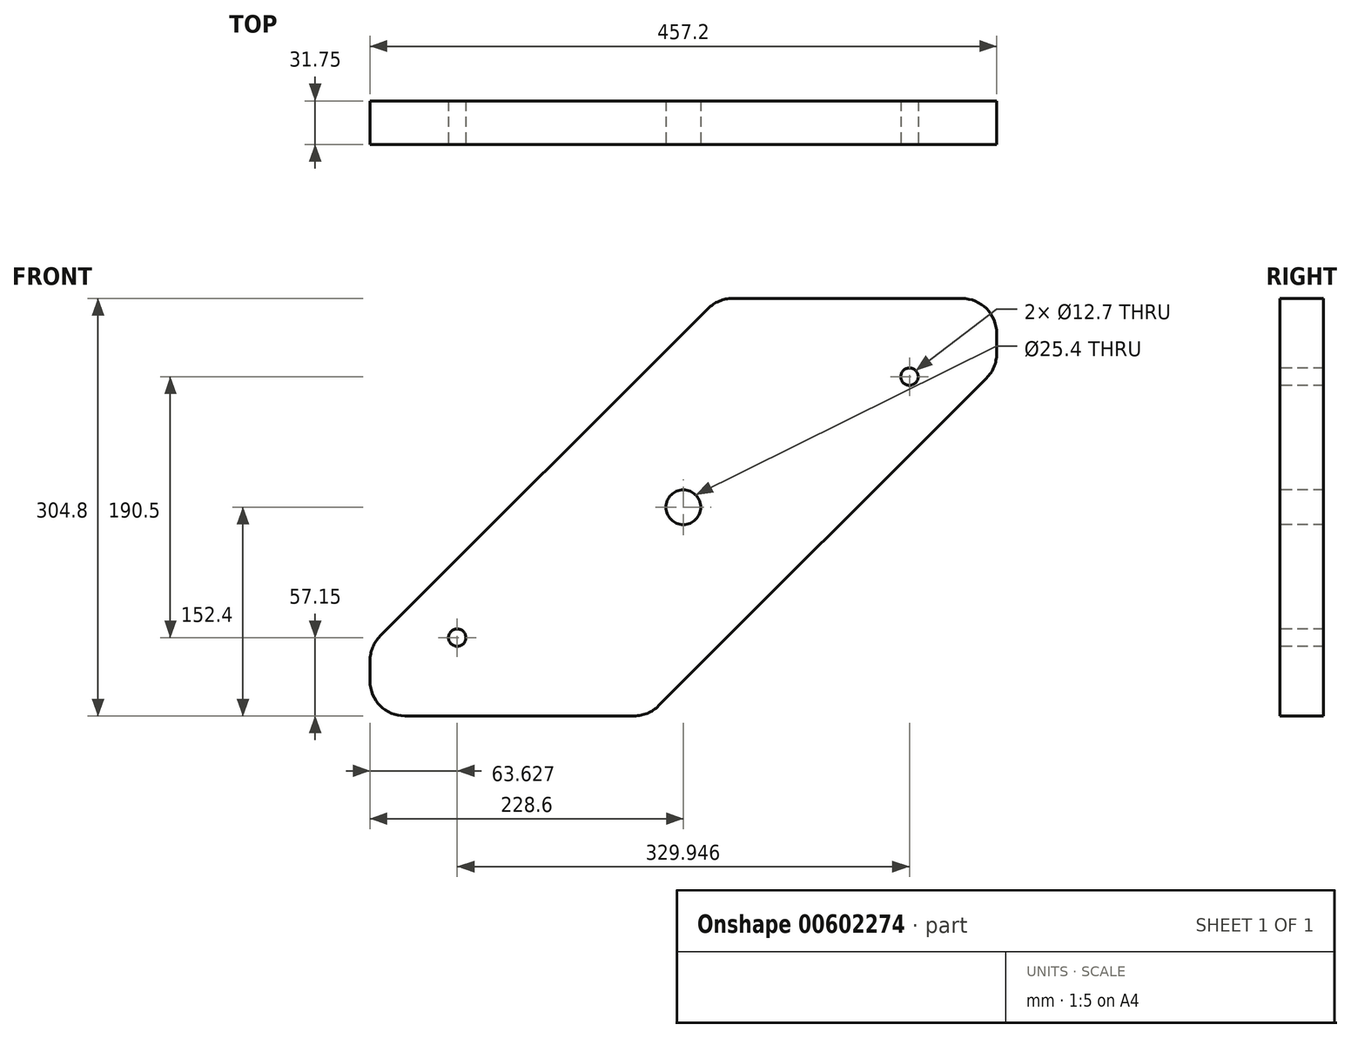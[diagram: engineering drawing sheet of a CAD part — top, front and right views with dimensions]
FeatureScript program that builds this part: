
annotation { "Feature Type Name" : "Feature", "Feature Type Description" : "" }
export const myFeature = defineFeature(function(context is Context, id is Id, definition is map)
    precondition{}
    {
        {
            var Q0;
            Q0=qCreatedBy(makeId("Front.planeOp"),FACE);
            var sketch = newSketch(context, id + "F0", { "sketchPlane" : qUnion([Q0])});
            skLineSegment(sketch, "E0.bottom", {"start": v(0, 0) * mm, "end": v(457.2, 0) * mm});
            skLineSegment(sketch, "E0.top", {"start": v(0, 304.8) * mm, "end": v(457.2, 304.8) * mm});
            skLineSegment(sketch, "E0.left", {"start": v(0, 0) * mm, "end": v(0, 304.8) * mm});
            skLineSegment(sketch, "E0.right", {"start": v(457.2, 0) * mm, "end": v(457.2, 304.8) * mm});
            skSolve(sketch);
        }
        {
            var Q0;
            Q0 = qSketchRegion(id + "F0", true);
            extrude(context, id + "F1", {"entities" : qUnion([Q0]), "depth" : 31.75 * mm, "offsetDistance" : 25.4 * mm});
        }
        {
            var Q0;
            Q0=makeQuery(id+"F1.opExtrude","SWEPT_EDGE",EDGE,{"disambiguationData":[OSD([sQuery(id+"F0.wireOp",EDGE,"E0.top"),sQuery(id+"F0.wireOp",EDGE,"E0.left")])]});
            var Q1;
            Q1=makeQuery(id+"F1.opExtrude","SWEPT_EDGE",EDGE,{"disambiguationData":[OSD([sQuery(id+"F0.wireOp",EDGE,"E0.bottom"),sQuery(id+"F0.wireOp",EDGE,"E0.right")])]});
            chamfer(context, id + "F2", {"entities" : qUnion([Q0, Q1]), "chamferType" : ChamferType.OFFSET_ANGLE, "width" : 254 * mm, "oppositeDirection" : false, "angle" : 45 * degree, "tangentPropagation" : true});
        }
        {
            var Q0;
            {var subQ0=sQuery(id+"F0.wireOp",EDGE,"E0.left");Q0=makeQuery(id+"F2.opChamfer","BLEND_EDGE",EDGE,{"blendedFrom":[makeQuery(id+"F1.opExtrude","SWEPT_EDGE",EDGE,{"disambiguationData":[OSD([sQuery(id+"F0.wireOp",EDGE,"E0.top"),subQ0])]}),makeQuery(id+"F1.opExtrude","SWEPT_FACE",FACE,{"disambiguationData":[OSD([subQ0])]})],"blendedInto":[makeQuery(id+"F1.opExtrude","SWEPT_FACE",FACE,{"disambiguationData":[OSD([subQ0])]})]});}
            var Q1;
            Q1=makeQuery(id+"F1.opExtrude","SWEPT_EDGE",EDGE,{"disambiguationData":[OSD([sQuery(id+"F0.wireOp",EDGE,"E0.bottom"),sQuery(id+"F0.wireOp",EDGE,"E0.left")])]});
            var Q2;
            {var subQ0=sQuery(id+"F0.wireOp",EDGE,"E0.bottom");Q2=makeQuery(id+"F2.opChamfer","BLEND_EDGE",EDGE,{"blendedFrom":[makeQuery(id+"F1.opExtrude","SWEPT_EDGE",EDGE,{"disambiguationData":[OSD([subQ0,sQuery(id+"F0.wireOp",EDGE,"E0.right")])]}),makeQuery(id+"F1.opExtrude","SWEPT_FACE",FACE,{"disambiguationData":[OSD([subQ0])]})],"blendedInto":[makeQuery(id+"F1.opExtrude","SWEPT_FACE",FACE,{"disambiguationData":[OSD([subQ0])]})]});}
            var Q3;
            {var subQ0=sQuery(id+"F0.wireOp",EDGE,"E0.right");Q3=makeQuery(id+"F2.opChamfer","BLEND_EDGE",EDGE,{"blendedFrom":[makeQuery(id+"F1.opExtrude","SWEPT_EDGE",EDGE,{"disambiguationData":[OSD([sQuery(id+"F0.wireOp",EDGE,"E0.bottom"),subQ0])]}),makeQuery(id+"F1.opExtrude","SWEPT_FACE",FACE,{"disambiguationData":[OSD([subQ0])]})],"blendedInto":[makeQuery(id+"F1.opExtrude","SWEPT_FACE",FACE,{"disambiguationData":[OSD([subQ0])]})]});}
            var Q4;
            Q4=makeQuery(id+"F1.opExtrude","SWEPT_EDGE",EDGE,{"disambiguationData":[OSD([sQuery(id+"F0.wireOp",EDGE,"E0.top"),sQuery(id+"F0.wireOp",EDGE,"E0.right")])]});
            var Q5;
            {var subQ0=sQuery(id+"F0.wireOp",EDGE,"E0.top");Q5=makeQuery(id+"F2.opChamfer","BLEND_EDGE",EDGE,{"blendedFrom":[makeQuery(id+"F1.opExtrude","SWEPT_EDGE",EDGE,{"disambiguationData":[OSD([subQ0,sQuery(id+"F0.wireOp",EDGE,"E0.left")])]}),makeQuery(id+"F1.opExtrude","SWEPT_FACE",FACE,{"disambiguationData":[OSD([subQ0])]})],"blendedInto":[makeQuery(id+"F1.opExtrude","SWEPT_FACE",FACE,{"disambiguationData":[OSD([subQ0])]})]});}
            fillet(context, id + "F3", {"entities" : qUnion([Q0, Q1, Q2, Q3, Q4, Q5]), "radius" : 25.4 * mm, "tangentPropagation" : true, "allowEdgeOverflow" : false});
        }
        {
            var Q0;
            Q0=makeQuery(id+"F1.opExtrude","CAP_FACE",FACE,{"disambiguationData":[OSD([sQuery(id+"F0.wireOp",EDGE,"E0.bottom"),sQuery(id+"F0.wireOp",EDGE,"E0.top"),sQuery(id+"F0.wireOp",EDGE,"E0.left"),sQuery(id+"F0.wireOp",EDGE,"E0.right")])],"isStart":false});
            var sketch = newSketch(context, id + "F4", { "sketchPlane" : qUnion([Q0])});
            skPoint(sketch, "E1", {"position": v(63.63, 57.15) * mm});
            skPoint(sketch, "E2", {"position": v(393.57, 247.65) * mm});
            skSolve(sketch);
        }
        {
            var Q0;
            Q0=sQuery(id+"F4.wireOp",VERTEX,"E1");
            var Q1;
            Q1=sQuery(id+"F4.wireOp",VERTEX,"E2");
            var Q2;
            Q2=makeQuery(id+"F1.opExtrude","SWEPT_BODY",BODY,{"disambiguationData":[OSD([sQuery(id+"F0.wireOp",EDGE,"E0.bottom"),sQuery(id+"F0.wireOp",EDGE,"E0.top"),sQuery(id+"F0.wireOp",EDGE,"E0.left"),sQuery(id+"F0.wireOp",EDGE,"E0.right")])]});
            hole(context, id + "F5", {"style" : HoleStyle.SIMPLE, "endStyle" : HoleEndStyle.THROUGH, "holeDiameter" : 12.7 * mm, "majorDiameter" : 6.35 * mm, "isTappedThrough" : true, "tappedDepth" : 12.7 * mm, "tapClearance" : 3, "locations" : qUnion([Q0, Q1]), "scope" : qUnion([Q2])});
        }
        {
            var Q0;
            Q0=makeQuery(id+"F1.opExtrude","CAP_FACE",FACE,{"disambiguationData":[OSD([sQuery(id+"F0.wireOp",EDGE,"E0.bottom"),sQuery(id+"F0.wireOp",EDGE,"E0.top"),sQuery(id+"F0.wireOp",EDGE,"E0.left"),sQuery(id+"F0.wireOp",EDGE,"E0.right")])],"isStart":false});
            var sketch = newSketch(context, id + "F6", { "sketchPlane" : qUnion([Q0])});
            skSolve(sketch);
        }
        {
            var Q0;
            {var subQ1=sQuery(id+"F0.wireOp",EDGE,"E0.top");Q0=makeQuery(id+"F6.imprint","IMPRINT",FACE,{"disambiguationData":[TD([[makeQuery(id+"F6.imprint","IMPRINT",EDGE,{"derivedFrom":makeQuery(id+"F1.opExtrude","CAP_EDGE",EDGE,{"disambiguationData":[OSD([subQ1])],"isStart":false})}),-1.0]])]});}
            var sketch = newSketch(context, id + "F7", { "sketchPlane" : qUnion([Q0])});
            skPoint(sketch, "E3", {"position": v(228.6, 152.4) * mm});
            skCircle(sketch, "E4", {"center": v(228.6, 152.4) * mm, "radius": 12.7 * mm});
            skSolve(sketch);
        }
        {
            var Q0;
            Q0=sQuery(id+"F7.wireOp",VERTEX,"E3");
            var Q1;
            Q1=makeQuery(id+"F1.opExtrude","SWEPT_BODY",BODY,{"disambiguationData":[OSD([sQuery(id+"F0.wireOp",EDGE,"E0.bottom"),sQuery(id+"F0.wireOp",EDGE,"E0.top"),sQuery(id+"F0.wireOp",EDGE,"E0.left"),sQuery(id+"F0.wireOp",EDGE,"E0.right")])]});
            hole(context, id + "F8", {"style" : HoleStyle.SIMPLE, "endStyle" : HoleEndStyle.THROUGH, "holeDiameter" : 25.4 * mm, "majorDiameter" : 6.35 * mm, "isTappedThrough" : true, "tappedDepth" : 12.7 * mm, "tapClearance" : 3, "locations" : qUnion([Q0]), "scope" : qUnion([Q1])});
        }
    });
